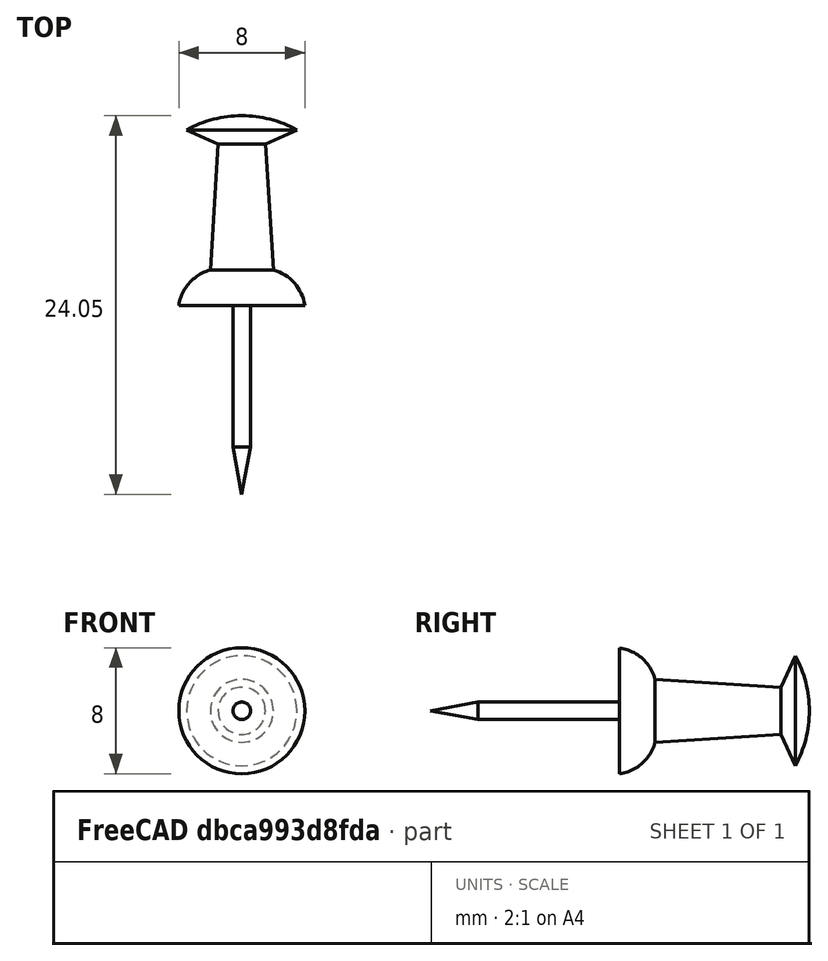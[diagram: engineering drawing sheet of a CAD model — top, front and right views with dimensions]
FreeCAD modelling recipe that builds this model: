
FCSTD DOCUMENT  (FreeCAD 0.17R13541 (Git))
Label: Chincheta
License: CreativeCommons Attribution
LicenseURL: http://creativecommons.org/licenses/by/4.0/
objects: Sketcher::SketchObject×1, PartDesign::Revolution×1, PartDesign::Body×1, Part::Feature×1
note: 5 computed .brp shape members not serialized (recipe doc carries the construction recipe); baked Part::Feature solids carry a one-line shape summary decoded from their .brp

FEATURE [Sketcher::SketchObject] Sketch  label="Perfil chincheta"
  MapMode = 5
  Support = -> [XY_Plane]
  sketch-geometry (14):
    g0: LineSegment StartX=0 StartY=0 StartZ=0 EndX=0.56 EndY=3 EndZ=0
    g1: LineSegment [constr] StartX=0.56 StartY=3 StartZ=0 EndX=0 EndY=3 EndZ=0
    g2: LineSegment [constr] StartX=0 StartY=12 StartZ=0 EndX=4 EndY=12 EndZ=0
    g3: LineSegment StartX=0.56 StartY=3 StartZ=0 EndX=0.56 EndY=12 EndZ=0
    g4: LineSegment StartX=0.56 StartY=12 StartZ=0 EndX=4 EndY=12 EndZ=0
    g5: ArcOfCircle CenterX=1.27984 CenterY=11.596 CenterZ=0 NormalX=0 NormalY=0 NormalZ=1 AngleXU=0 Radius=2.75 StartAngle=0.147454 EndAngle=1.30583
    g6: LineSegment [constr] StartX=0 StartY=14.25 StartZ=0 EndX=2 EndY=14.25 EndZ=0
    g7: LineSegment [constr] StartX=0 StartY=22.25 StartZ=0 EndX=1.5 EndY=22.25 EndZ=0
    g8: LineSegment StartX=1.5 StartY=22.25 StartZ=0 EndX=2 EndY=14.25 EndZ=0
    g9: LineSegment [constr] StartX=0 StartY=23.15 StartZ=0 EndX=3.5 EndY=23.15 EndZ=0
    g10: LineSegment StartX=1.5 StartY=22.25 StartZ=0 EndX=3.5 EndY=23.15 EndZ=0
    g11: LineSegment [constr] StartX=0 StartY=24.05 StartZ=0 EndX=7 EndY=24.05 EndZ=0
    g12: ArcOfCircle CenterX=0 CenterY=16.7944 CenterZ=0 NormalX=0 NormalY=0 NormalZ=1 AngleXU=0 Radius=7.25556 StartAngle=1.06742 EndAngle=1.5708
    g13: LineSegment StartX=0 StartY=24.05 StartZ=0 EndX=0 EndY=0 EndZ=0
  constraints (44):
    c: Coincident(g0,g-1)
    c: Horizontal(g1)
    c: DistanceX(g1,g1) = 0.56
    c: PointOnObject(g1,g-2)
    c: Distance(g-1,g1) = 3
    c: Horizontal(g2)
    c: DistanceX(g2,g2) = 4
    c: PointOnObject(g2,g-2)
    c: Distance(g2,g1) = 9
    c: Vertical(g3)
    c: Coincident(g0,g1)
    c: Coincident(g0,g3)
    c: PointOnObject(g3,g2)
    c: Horizontal(g4)
    c: Coincident(g3,g4)
    c: Coincident(g2,g4)
    c: Coincident(g2,g5)
    c: Horizontal(g6)
    c: DistanceX(g6,g6) = 2
    c: PointOnObject(g6,g-2)
    c: Distance(g6,g2) = 2.25
    c: Coincident(g5,g6)
    c: Radius(g5) = 2.75
    c: Horizontal(g7)
    c: DistanceX(g7,g7) = 1.5
    c: PointOnObject(g7,g-2)
    c: Distance(g7,g6) = 8
    c: Coincident(g5,g8)
    c: Coincident(g7,g8)
    c: Horizontal(g9)
    c: DistanceX(g9,g9) = 3.5
    c: PointOnObject(g9,g-2)
    c: Distance(g9,g7) = 0.9
    c: Coincident(g7,g10)
    c: Coincident(g9,g10)
    c: Horizontal(g11)
    c: DistanceX(g11,g11) = 7
    c: PointOnObject(g11,g-2)
    c: Distance(g11,g9) = 0.9
    c: Coincident(g9,g12)
    c: Tangent(g11,g12) = 1.5708
    c: Vertical(g13)
    c: Coincident(g0,g13)
    c: Coincident(g11,g13)
FEATURE [PartDesign::Revolution] Revolution  label="Master chincheta"
  Angle = 360
  Axis = (0,1,0)
  Base = (0,0,0)
  Profile = -> Sketch
  ReferenceAxis = -> Sketch [V_Axis]
  Reversed = true
FEATURE [PartDesign::Body] Body
  Group = -> [Sketch,Revolution]
  Origin = -> Origin
  Tip = -> Revolution
FEATURE [Part::Feature] Revolution001  label="Chincheta"
  shape: bbox 8 x 24.05 x 8 mm, 7 faces (baked)
